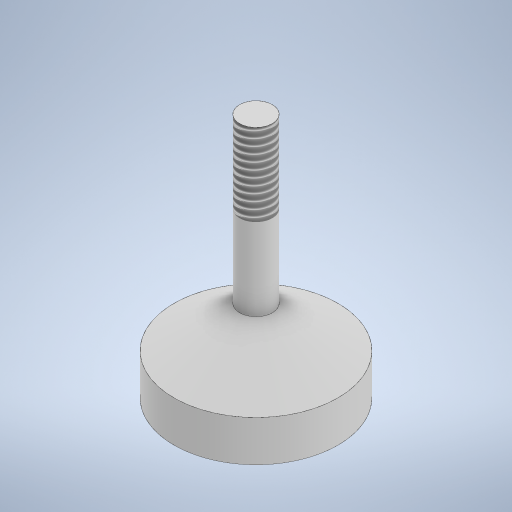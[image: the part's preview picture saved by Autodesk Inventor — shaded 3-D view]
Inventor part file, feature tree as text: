
AUTODESK INVENTOR PART (.ipt)
format: ipt  version: 2023 (Build 270158030, 158C)  size: 254,976 bytes
history: native  units: in
note: dims shown in document units (in); Inventor stores cm internally (conversion verified against a paired STEP export)
features: revolve x1, thread x1, sketch x1
ambient origin geometry x8: Origin, YZ Plane, XZ Plane, XY Plane, X Axis, Y Axis, Z Axis, Center Point
bodies: Solid1 (feature_tree)
feature tree (3):
  revolve  "Revolution1"  [1 undecoded]
  thread  "Thread1"  [1 undecoded]
  sketch  "Sketch1"  dims[d0=0.5in d1=0.25in d2=0.25in d3=0.1in d4=1.0in d5=90.0deg d6=0.5in d7=0.0in]
note: 2 required parameter values undecoded (feature->parameter linkage not recoverable at this tier; creation-order binding heuristic only, values carry confidence <= 0.55)